# Revit family: NBS_Allermuir_IntPlntrSym_Crate_Planter
name_source: partatom
category: Furniture
revit_build: Autodesk Revit 2018 (Build: 20190510_1515(x64)
units: mm (PartAtom-declared; Revit-internal decimal feet)

## family parameters
Always vertical = Yes
Cut with Voids When Loaded = No
Room Calculation Point = No
Shared = No
Work Plane-Based = No

## types (1)
- Crate_Planter_CRT6020
    AssetType = Movable
    BIMObjectName = NBS_Allermuir_InternalPlanterSystem_Crate_Planter_CRT6020
    Category = Ss_45_40_40_42:Internal planter systems
    Color = Black, Pebble, Sage
    Description = Planter
    DurationUnit = year
    ExpectedLife = 10
    Features = 25mm Laminate faced MDF core top, Edge detail with a clear finish, Steel pedestal base finished in Silver powder coat, Plastic glides, Steel frame and box insert available in a selection of powder coat finishes
    Finish = Black, Pebble, Sage
    Frame = Steel
    FrameMaterial = NBS_Allermuir_Steel_BlackPowderCoat
    IfcExportAs = IfcFurnitureType
    IfcExportType = USERDEFINED
    IsBuiltIn = No
    ManufacturerName = Allermuir
    ManufacturerURL = www.allermuir.co.uk
    Material = Steel, Solid Wood
    ModelNumber = CRT6020
    ModelReference = Crate_Planter
    NBSCertification = www.nationalbimlibrary.com/cert/j5y1ylct
    NBSDescription = Internal planter system
    NBSReference = 40-40-40/165
    Name = InternalPlanterSystem_CRT6020_Crate_Allermuir
    NominalDepth = 250 mm
    NominalHeight = 630 mm
    NominalLength = 600 mm
    NominalWidth = 600 mm
    ProductInformation = https://www.allermuir.com
    Size = 250 x 630 x 600mm
    Status = UNSET
    Style = Planter
    SustainabilityPerformance = 13.5% recyclable
    TopShelfMaterial = NBS_Allermuir_Oak_ClearFinish
    Uniclass2015Code = Ss_45_40_40_42
    Uniclass2015Title = Internal planter systems
    Uniclass2015Version = Systems v1.15
    Version = 1
    WarrantyDescription = Allermuir warrant that its manufactured products are free from manufacturing defects - in materials or workmanship - for a period of five (5) years. , Allermuir will repair, or replace (at Allermuir's sole discretion) with comparable free of charge materials / components, any product / component which fails under normal use in a single shift environment, as a result of a defect in the materials and/ or workmanship
    WarrantyDurationParts = 5
    WarrantyDurationUnit = year

## geometry (parser evidence)
native form markers: Sweep x2
no freeform markers — native parametric forms only
